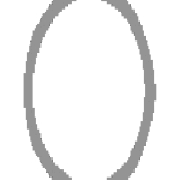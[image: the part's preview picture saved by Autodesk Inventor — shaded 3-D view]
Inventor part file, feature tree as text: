
AUTODESK INVENTOR PART (.ipt)
format: ipt  version: 2021 (Build 250183000, 183)  size: 114,176 bytes
history: native  units: in
note: dims shown in document units (in); Inventor stores cm internally (conversion verified against a paired STEP export)
features: other x4, sketch x3, plane x1
ambient origin geometry x8: Origin, YZ Plane, XZ Plane, XY Plane, X Axis, Y Axis, Z Axis, Center Point
bodies: Solid1 (feature_tree), Body (feature_tree)
feature tree (8):
  other  "Driven Length"
  other  "Frame Generator"
  other  "Start Plane"
  other  "End Plane"
  sketch  "Sketch"  dims[d2=6.7082in d4=-0.0in d5=6.7082in d6=0.12in d7=0.0in d8=90.0deg d9=6.7082in]
  sketch  "Sketch2"  dims[d0=1.0in]
  plane  "Work Plane3"
  sketch  "Sketch3"  dims[d1=0.065in]
